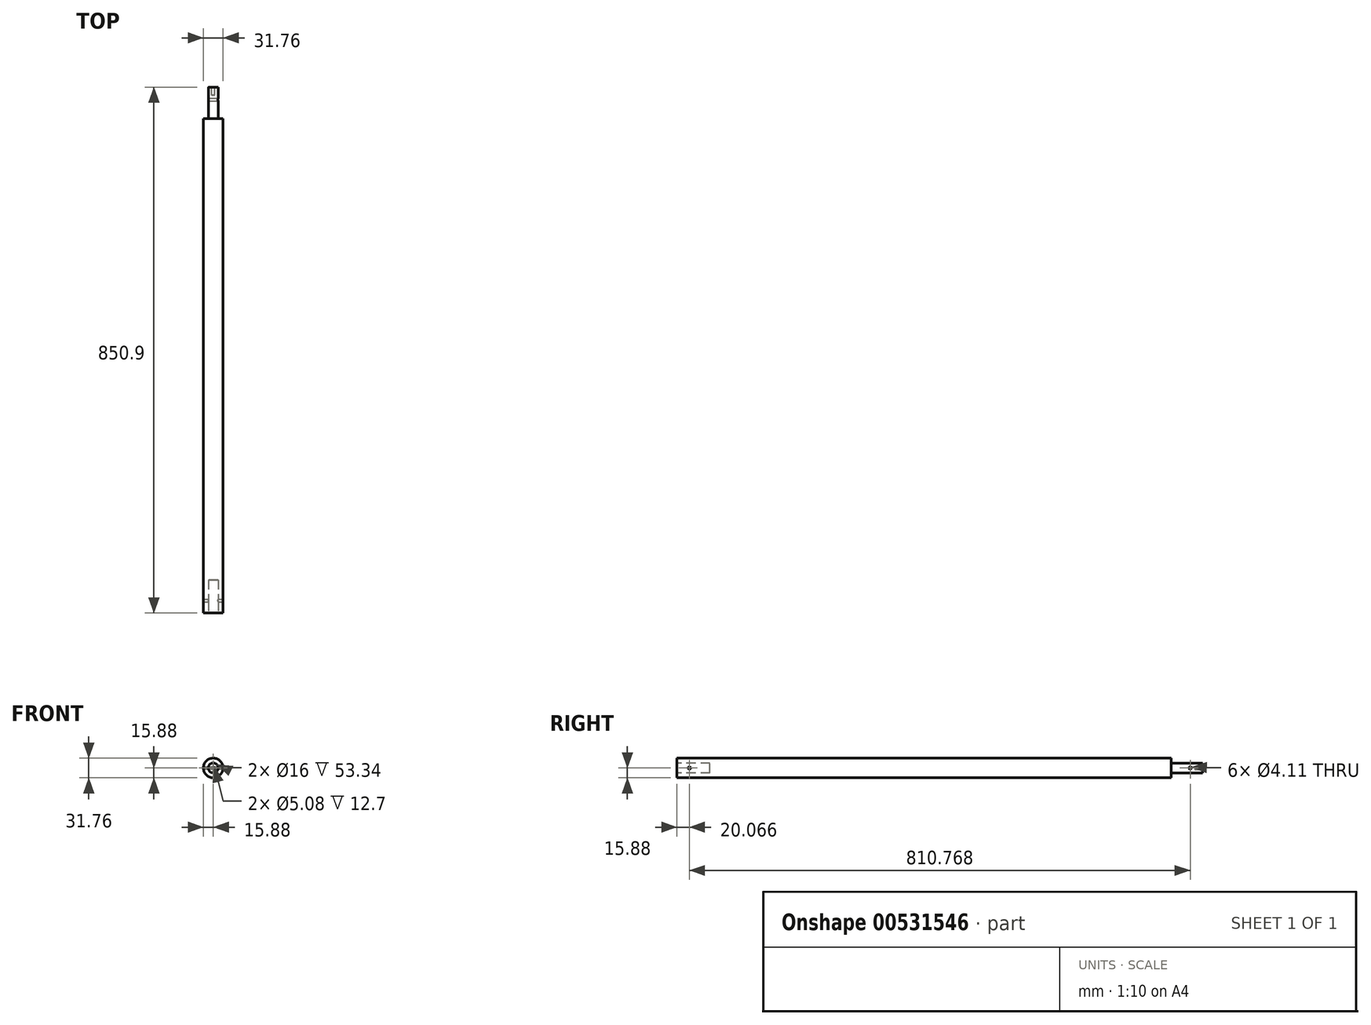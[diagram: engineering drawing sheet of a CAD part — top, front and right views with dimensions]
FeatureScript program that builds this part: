
annotation { "Feature Type Name" : "Feature", "Feature Type Description" : "" }
export const myFeature = defineFeature(function(context is Context, id is Id, definition is map)
    precondition{}
    {
        {
            var Q0;
            Q0=qCreatedBy(makeId("Front.planeOp"),FACE);
            var sketch = newSketch(context, id + "F0", { "sketchPlane" : qUnion([Q0])});
            skCircle(sketch, "E0", {"center": v(0, 0) * mm, "radius": 15.88 * mm});
            skSolve(sketch);
        }
        {
            var Q0;
            Q0 = qSketchRegion(id + "F0", true);
            extrude(context, id + "F1", {"entities" : qUnion([Q0]), "depth" : 850.9 * mm, "offsetDistance" : 25.4 * mm});
        }
        {
            var Q0;
            Q0=makeQuery(id+"F1.opExtrude","CAP_FACE",FACE,{"disambiguationData":[OSD([sQuery(id+"F0.wireOp",EDGE,"E0")])],"isStart":false});
            var sketch = newSketch(context, id + "F2", { "sketchPlane" : qUnion([Q0])});
            skCircle(sketch, "E1", {"center": v(0, 0) * mm, "radius": 8 * mm});
            skSolve(sketch);
        }
        {
            var Q0;
            Q0 = qSketchRegion(id + "F2", true);
            extrude(context, id + "F3", {"entities" : qUnion([Q0]), "operationType" : NewBodyOperationType.REMOVE, "oppositeDirection" : true, "depth" : 53.34 * mm, "offsetDistance" : 25.4 * mm});
        }
        {
            var Q0;
            Q0=qCreatedBy(makeId("Right.planeOp"),FACE);
            var sketch = newSketch(context, id + "F4", { "sketchPlane" : qUnion([Q0])});
            skCircle(sketch, "E2", {"center": v(-830.83, 0) * mm, "radius": 2.06 * mm});
            skLineSegment(sketch, "E3.0", {"start": v(-850.9, -15.88) * mm, "end": v(-850.9, 15.88) * mm});
            skLineSegment(sketch, "E4", {"start": v(0, -15.88) * mm, "end": v(-792.48, -15.88) * mm});
            skLineSegment(sketch, "E5", {"start": v(-792.48, 15.88) * mm, "end": v(0, 15.88) * mm});
            skCircle(sketch, "E6", {"center": v(-20.07, 0) * mm, "radius": 2.06 * mm});
            skSolve(sketch);
        }
        {
            var Q0;
            Q0 = qSketchRegion(id + "F4", true);
            extrude(context, id + "F5", {"entities" : qUnion([Q0]), "operationType" : NewBodyOperationType.REMOVE, "endBound" : BoundingType.SYMMETRIC, "oppositeDirection" : true, "depth" : 50.8 * mm, "offsetDistance" : 25.4 * mm});
        }
        {
            var Q0;
            Q0=makeQuery(id+"F1.opExtrude","CAP_FACE",FACE,{"disambiguationData":[OSD([sQuery(id+"F0.wireOp",EDGE,"E0")])],"isStart":true});
            var sketch = newSketch(context, id + "F6", { "sketchPlane" : qUnion([Q0])});
            skCircle(sketch, "E7.0", {"center": v(0, 0) * mm, "radius": 15.88 * mm});
            skCircle(sketch, "E8", {"center": v(0, 0) * mm, "radius": 7.99 * mm});
            skSolve(sketch);
        }
        {
            var Q0;
            Q0 = qSketchRegion(id + "F6", true);
            extrude(context, id + "F7", {"entities" : qUnion([Q0]), "operationType" : NewBodyOperationType.REMOVE, "oppositeDirection" : true, "depth" : 50.8 * mm, "offsetDistance" : 25.4 * mm});
        }
        {
            var Q0;
            Q0=makeQuery(id+"F1.opExtrude","CAP_FACE",FACE,{"disambiguationData":[OSD([sQuery(id+"F0.wireOp",EDGE,"E0")])],"isStart":true});
            var sketch = newSketch(context, id + "F8", { "sketchPlane" : qUnion([Q0])});
            skCircle(sketch, "E9", {"center": v(0, 0) * mm, "radius": 2.54 * mm});
            skSolve(sketch);
        }
        {
            var Q0;
            Q0 = qSketchRegion(id + "F8", true);
            extrude(context, id + "F9", {"entities" : qUnion([Q0]), "operationType" : NewBodyOperationType.REMOVE, "oppositeDirection" : true, "depth" : 12.7 * mm, "offsetDistance" : 25.4 * mm});
        }
    });
